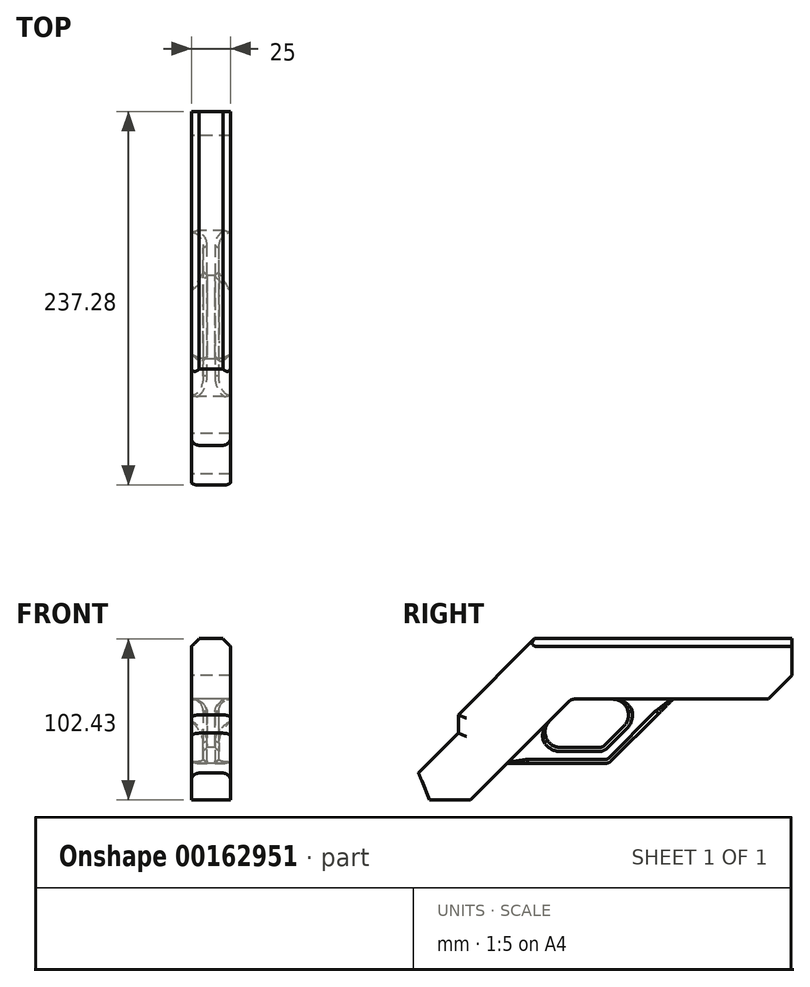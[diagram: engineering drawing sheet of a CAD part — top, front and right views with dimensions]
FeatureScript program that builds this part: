
annotation { "Feature Type Name" : "Feature", "Feature Type Description" : "" }
export const myFeature = defineFeature(function(context is Context, id is Id, definition is map)
    precondition{}
    {
        {
            var Q0;
            Q0=qCreatedBy(makeId("Right.planeOp"),FACE);
            var sketch = newSketch(context, id + "F0", { "sketchPlane" : qUnion([Q0])});
            skLineSegment(sketch, "E0", {"start": v(-96.29, 0) * mm, "end": v(-96.29, 15) * mm});
            skLineSegment(sketch, "E1", {"start": v(-96.29, 15) * mm, "end": v(75.64, 15) * mm});
            skLineSegment(sketch, "E2", {"start": v(75.64, 15) * mm, "end": v(75.64, 0) * mm});
            skLineSegment(sketch, "E3", {"start": v(75.64, 0) * mm, "end": v(60.55, -15) * mm});
            skLineSegment(sketch, "E4", {"start": v(60.55, -15) * mm, "end": v(0, -15) * mm});
            skLineSegment(sketch, "E5", {"start": v(0, -15) * mm, "end": v(-10, -25) * mm});
            skLineSegment(sketch, "E6", {"start": v(-10, -25) * mm, "end": v(-96.29, -25) * mm});
            skLineSegment(sketch, "E7", {"start": v(-96.29, -25) * mm, "end": v(-96.29, 0) * mm});
            skLineSegment(sketch, "E8", {"start": v(-96.29, 15) * mm, "end": v(-136.29, -25) * mm});
            skLineSegment(sketch, "E9", {"start": v(-136.29, -25) * mm, "end": v(-136.29, -36.6) * mm});
            skLineSegment(sketch, "E10", {"start": v(-136.29, -36.6) * mm, "end": v(-178.71, -79.02) * mm});
            skLineSegment(sketch, "E11", {"start": v(-178.71, -79.02) * mm, "end": v(-128.71, -79.02) * mm});
            skLineSegment(sketch, "E12", {"start": v(-128.71, -79.02) * mm, "end": v(-74.7, -25) * mm});
            skLineSegment(sketch, "E13", {"start": v(-10, -25) * mm, "end": v(-40.76, -55.76) * mm});
            skLineSegment(sketch, "E14", {"start": v(-40.76, -55.76) * mm, "end": v(-105.46, -55.76) * mm});
            skLineSegment(sketch, "E15", {"start": v(-24.14, -25) * mm, "end": v(-44.9, -45.76) * mm});
            skLineSegment(sketch, "E16", {"start": v(-44.9, -45.76) * mm, "end": v(-95.46, -45.76) * mm});
            skLineSegment(sketch, "E17", {"start": v(-96.29, 15) * mm, "end": v(-87.88, 23.41) * mm});
            skLineSegment(sketch, "E18", {"start": v(-87.88, 23.41) * mm, "end": v(75.64, 23.41) * mm});
            skLineSegment(sketch, "E19", {"start": v(75.64, 23.41) * mm, "end": v(75.64, 15) * mm});
            skLineSegment(sketch, "E20", {"start": v(-74.7, -25) * mm, "end": v(-64.7, -15) * mm});
            skLineSegment(sketch, "E21", {"start": v(-64.7, -15) * mm, "end": v(0, -15) * mm});
            skLineSegment(sketch, "E22", {"start": v(-24.14, -25) * mm, "end": v(-14.14, -15) * mm});
            skSolve(sketch);
        }
        {
            var Q0;
            Q0=makeQuery(id+"F0.imprint","IMPRINT",FACE,{"disambiguationData":[TD([[makeQuery(id+"F0.imprint","IMPRINT",EDGE,{"derivedFrom":sQuery(id+"F0.wireOp",EDGE,"E0")}),1.0]])]});
            var Q1;
            Q1=makeQuery(id+"F0.imprint","IMPRINT",FACE,{"disambiguationData":[TD([[makeQuery(id+"F0.imprint","IMPRINT",EDGE,{"derivedFrom":sQuery(id+"F0.wireOp",EDGE,"E0")}),-1.0]])]});
            var Q2;
            {var subQ1=sQuery(id+"F0.wireOp",EDGE,"E13");Q2=makeQuery(id+"F0.imprint","IMPRINT",FACE,{"disambiguationData":[TD([[makeQuery(id+"F0.imprint","IMPRINT",EDGE,{"derivedFrom":subQ1}),-1.0]])]});}
            var Q3;
            Q3=makeQuery(id+"F0.imprint","IMPRINT",FACE,{"disambiguationData":[TD([[makeQuery(id+"F0.imprint","IMPRINT",EDGE,{"derivedFrom":sQuery(id+"F0.wireOp",EDGE,"E1")}),1.0]])]});
            var Q4;
            {var subQ0=sQuery(id+"F0.wireOp",EDGE,"E5");Q4=makeQuery(id+"F0.imprint","IMPRINT",FACE,{"disambiguationData":[TD([[makeQuery(id+"F0.imprint","IMPRINT",EDGE,{"derivedFrom":subQ0}),-1.0]])]});}
            extrude(context, id + "F1", {"entities" : qUnion([Q0, Q1, Q2, Q3, Q4]), "depth" : 12.5 * mm});
        }
        {
            var Q0;
            Q0=makeQuery(id+"F1.opExtrude","CAP_EDGE",EDGE,{"disambiguationData":[OSD([sQuery(id+"F0.wireOp",EDGE,"E18")])],"isStart":false});
            chamfer(context, id + "F2", {"entities" : qUnion([Q0]), "width" : 5 * mm, "tangentPropagation" : true});
        }
        {
            var Q0;
            {var subQ0=makeQuery(id+"F1.opExtrude","SWEPT_EDGE",EDGE,{"disambiguationData":[OSD([sQuery(id+"F0.wireOp",EDGE,"E10"),sQuery(id+"F0.wireOp",EDGE,"E11")])]});Q0=makeQuery(id+"F9.boolean.opBoolean","MERGE",EDGE,{"derivedFrom":[subQ0,makeQuery(id+"F9.opPattern","COPY",EDGE,{"derivedFrom":subQ0,"instanceName":"1"})]});}
            chamfer(context, id + "F3", {"entities" : qUnion([Q0]), "width" : 10 * mm, "tangentPropagation" : true});
        }
        {
            var Q0;
            {var subQ0=makeQuery(id+"F1.opExtrude","SWEPT_EDGE",EDGE,{"disambiguationData":[OSD([sQuery(id+"F0.wireOp",EDGE,"E12"),sQuery(id+"F0.wireOp",EDGE,"E16")])]});Q0=makeQuery(id+"F9.boolean.opBoolean","MERGE",EDGE,{"derivedFrom":[subQ0,makeQuery(id+"F9.opPattern","COPY",EDGE,{"derivedFrom":subQ0,"instanceName":"1"})]});}
            var Q1;
            {var subQ0=makeQuery(id+"F1.opExtrude","SWEPT_EDGE",EDGE,{"disambiguationData":[OSD([sQuery(id+"F0.wireOp",EDGE,"E21"),sQuery(id+"F0.wireOp",EDGE,"E22")])]});Q1=makeQuery(id+"F9.boolean.opBoolean","MERGE",EDGE,{"derivedFrom":[subQ0,makeQuery(id+"F9.opPattern","COPY",EDGE,{"derivedFrom":subQ0,"instanceName":"1"})]});}
            fillet(context, id + "F4", {"entities" : qUnion([Q0, Q1]), "radius" : 10 * mm, "tangentPropagation" : true, "allowEdgeOverflow" : false});
        }
        {
            var Q0;
            Q0=makeQuery(id+"F1.opExtrude","CAP_FACE",FACE,{"disambiguationData":[OSD([sQuery(id+"F0.wireOp",EDGE,"E2"),sQuery(id+"F0.wireOp",EDGE,"E3"),sQuery(id+"F0.wireOp",EDGE,"E4"),sQuery(id+"F0.wireOp",EDGE,"E5"),sQuery(id+"F0.wireOp",EDGE,"E8"),sQuery(id+"F0.wireOp",EDGE,"E9"),sQuery(id+"F0.wireOp",EDGE,"E10"),sQuery(id+"F0.wireOp",EDGE,"E11"),sQuery(id+"F0.wireOp",EDGE,"E12"),sQuery(id+"F0.wireOp",EDGE,"E13"),sQuery(id+"F0.wireOp",EDGE,"E14"),sQuery(id+"F0.wireOp",EDGE,"E15"),sQuery(id+"F0.wireOp",EDGE,"E16"),sQuery(id+"F0.wireOp",EDGE,"E17"),sQuery(id+"F0.wireOp",EDGE,"E18"),sQuery(id+"F0.wireOp",EDGE,"E19"),sQuery(id+"F0.wireOp",EDGE,"E20"),sQuery(id+"F0.wireOp",EDGE,"E21"),sQuery(id+"F0.wireOp",EDGE,"E22")])],"isStart":false});
            var sketch = newSketch(context, id + "F5", { "sketchPlane" : qUnion([Q0])});
            skLineSegment(sketch, "E23.0", {"start": v(-128.71, -79.02) * mm, "end": v(-105.46, -55.76) * mm});
            skLineSegment(sketch, "E24.0", {"start": v(-40.76, -55.76) * mm, "end": v(-105.46, -55.76) * mm});
            skLineSegment(sketch, "E25.0", {"start": v(0, -15) * mm, "end": v(-40.76, -55.76) * mm});
            skLineSegment(sketch, "E26.0", {"start": v(-78.39, -28.7) * mm, "end": v(-64.7, -15) * mm});
            skLineSegment(sketch, "E27", {"start": v(-105.46, -55.76) * mm, "end": v(-78.39, -28.7) * mm});
            skLineSegment(sketch, "E28", {"start": v(-64.7, -15) * mm, "end": v(0, -15) * mm});
            skSolve(sketch);
        }
        {
            var Q0;
            Q0=makeQuery(id+"F5.imprint","IMPRINT",FACE,{"disambiguationData":[TD([[makeQuery(id+"F5.imprint","IMPRINT",EDGE,{"derivedFrom":sQuery(id+"F5.wireOp",EDGE,"E24.0")}),-1.0]])]});
            extrude(context, id + "F6", {"entities" : qUnion([Q0]), "operationType" : NewBodyOperationType.REMOVE, "oppositeDirection" : true, "depth" : 7.5 * mm});
        }
        {
            var Q0;
            {var subQ0=sQuery(id+"F0.wireOp",EDGE,"E12");Q0=makeQuery(id+"F6.boolean.opBoolean","MERGE",EDGE,{"derivedFrom":[makeQuery(id+"F1.opExtrude","CAP_EDGE",EDGE,{"disambiguationData":[OSD([subQ0])],"isStart":false}),makeQuery(id+"F1.opExtrude","CAP_EDGE",EDGE,{"disambiguationData":[OSD([subQ0,sQuery(id+"F0.wireOp",EDGE,"E20")])],"isStart":false}),makeQuery(id+"F6.opExtrude","CAP_EDGE",EDGE,{"disambiguationData":[OSD([sQuery(id+"F5.wireOp",EDGE,"E27")])],"isStart":true})]});}
            var Q1;
            Q1=makeQuery(id+"F1.opExtrude","CAP_EDGE",EDGE,{"disambiguationData":[OSD([sQuery(id+"F0.wireOp",EDGE,"E10")])],"isStart":false});
            var Q2;
            Q2=makeQuery(id+"F1.opExtrude","CAP_EDGE",EDGE,{"disambiguationData":[OSD([sQuery(id+"F0.wireOp",EDGE,"E9")])],"isStart":false});
            var Q3;
            Q3=makeQuery(id+"F1.opExtrude","CAP_EDGE",EDGE,{"disambiguationData":[OSD([sQuery(id+"F0.wireOp",EDGE,"E8"),sQuery(id+"F0.wireOp",EDGE,"E17")])],"isStart":false});
            fillet(context, id + "F7", {"entities" : qUnion([Q0, Q1, Q2, Q3]), "radius" : 5 * mm, "tangentPropagation" : true, "allowEdgeOverflow" : false});
        }
        {
            var Q0;
            Q0=makeQuery(id+"F1.opExtrude","SWEPT_EDGE",EDGE,{"disambiguationData":[OSD([sQuery(id+"F0.wireOp",EDGE,"E13"),sQuery(id+"F0.wireOp",EDGE,"E14")])]});
            var Q1;
            Q1=makeQuery(id+"F1.opExtrude","SWEPT_EDGE",EDGE,{"disambiguationData":[OSD([sQuery(id+"F0.wireOp",EDGE,"E15"),sQuery(id+"F0.wireOp",EDGE,"E16")])]});
            var Q2;
            Q2=makeQuery(id+"F1.opExtrude","SWEPT_EDGE",EDGE,{"disambiguationData":[OSD([sQuery(id+"F0.wireOp",EDGE,"E20"),sQuery(id+"F0.wireOp",EDGE,"E21")])]});
            fillet(context, id + "F8", {"entities" : qUnion([Q0, Q1, Q2]), "radius" : 5 * mm, "tangentPropagation" : true, "allowEdgeOverflow" : false});
        }
        {
            var Q0;
            Q0=makeQuery(id+"F1.opExtrude","SWEPT_BODY",BODY,{"disambiguationData":[OSD([sQuery(id+"F0.wireOp",EDGE,"E1"),sQuery(id+"F0.wireOp",EDGE,"E2"),sQuery(id+"F0.wireOp",EDGE,"E3"),sQuery(id+"F0.wireOp",EDGE,"E4"),sQuery(id+"F0.wireOp",EDGE,"E5"),sQuery(id+"F0.wireOp",EDGE,"E6"),sQuery(id+"F0.wireOp",EDGE,"E8"),sQuery(id+"F0.wireOp",EDGE,"E9"),sQuery(id+"F0.wireOp",EDGE,"E10"),sQuery(id+"F0.wireOp",EDGE,"E11"),sQuery(id+"F0.wireOp",EDGE,"E12"),sQuery(id+"F0.wireOp",EDGE,"E13"),sQuery(id+"F0.wireOp",EDGE,"E14"),sQuery(id+"F0.wireOp",EDGE,"E15"),sQuery(id+"F0.wireOp",EDGE,"E16")])]});
            var Q1;
            Q1=qCreatedBy(makeId("Right.planeOp"),FACE);
            mirror(context, id + "F9", {"operationType" : NewBodyOperationType.ADD, "entities" : qUnion([Q0]), "mirrorPlane" : qUnion([Q1])});
        }
        {
            var Q0;
            Q0=makeQuery(id+"F6.boolean.opBoolean","COPY",EDGE,{"derivedFrom":makeQuery(id+"F6.opExtrude","CAP_EDGE",EDGE,{"disambiguationData":[OSD([sQuery(id+"F5.wireOp",EDGE,"E27")])],"isStart":false})});
            var Q1;
            Q1=makeQuery(id+"F9.opPattern","COPY",EDGE,{"derivedFrom":makeQuery(id+"F6.boolean.opBoolean","COPY",EDGE,{"derivedFrom":makeQuery(id+"F6.opExtrude","CAP_EDGE",EDGE,{"disambiguationData":[OSD([sQuery(id+"F5.wireOp",EDGE,"E27")])],"isStart":false})}),"instanceName":"1"});
            var Q2;
            Q2=makeQuery(id+"F9.opPattern","COPY",EDGE,{"derivedFrom":makeQuery(id+"F6.boolean.opBoolean","COPY",EDGE,{"derivedFrom":makeQuery(id+"F6.opExtrude","CAP_EDGE",EDGE,{"disambiguationData":[OSD([sQuery(id+"F5.wireOp",EDGE,"E28")])],"isStart":false})}),"instanceName":"1"});
            var Q3;
            Q3=makeQuery(id+"F6.boolean.opBoolean","COPY",EDGE,{"derivedFrom":makeQuery(id+"F6.opExtrude","CAP_EDGE",EDGE,{"disambiguationData":[OSD([sQuery(id+"F5.wireOp",EDGE,"E28")])],"isStart":false})});
            fillet(context, id + "F10", {"entities" : qUnion([Q0, Q1, Q2, Q3]), "radius" : 7.5 * mm, "tangentPropagation" : true, "allowEdgeOverflow" : false});
        }
        {
            var Q0;
            Q0=makeQuery(id+"F6.boolean.opBoolean","COPY",FACE,{"derivedFrom":makeQuery(id+"F6.opExtrude","CAP_FACE",FACE,{"disambiguationData":[OSD([sQuery(id+"F0.wireOp",EDGE,"E2"),sQuery(id+"F0.wireOp",EDGE,"E3"),sQuery(id+"F0.wireOp",EDGE,"E4"),sQuery(id+"F0.wireOp",EDGE,"E5"),sQuery(id+"F0.wireOp",EDGE,"E8"),sQuery(id+"F0.wireOp",EDGE,"E9"),sQuery(id+"F0.wireOp",EDGE,"E10"),sQuery(id+"F0.wireOp",EDGE,"E11"),sQuery(id+"F0.wireOp",EDGE,"E12"),sQuery(id+"F0.wireOp",EDGE,"E13"),sQuery(id+"F0.wireOp",EDGE,"E14"),sQuery(id+"F0.wireOp",EDGE,"E15"),sQuery(id+"F0.wireOp",EDGE,"E16"),sQuery(id+"F0.wireOp",EDGE,"E17"),sQuery(id+"F0.wireOp",EDGE,"E18"),sQuery(id+"F0.wireOp",EDGE,"E19"),sQuery(id+"F0.wireOp",EDGE,"E20"),sQuery(id+"F0.wireOp",EDGE,"E21"),sQuery(id+"F0.wireOp",EDGE,"E22"),sQuery(id+"F5.wireOp",EDGE,"E24.0"),sQuery(id+"F5.wireOp",EDGE,"E25.0"),sQuery(id+"F5.wireOp",EDGE,"E27"),sQuery(id+"F5.wireOp",EDGE,"E28")])],"isStart":false})});
            var Q1;
            Q1=makeQuery(id+"F9.opPattern","COPY",FACE,{"derivedFrom":makeQuery(id+"F6.boolean.opBoolean","COPY",FACE,{"derivedFrom":makeQuery(id+"F6.opExtrude","CAP_FACE",FACE,{"disambiguationData":[OSD([sQuery(id+"F0.wireOp",EDGE,"E2"),sQuery(id+"F0.wireOp",EDGE,"E3"),sQuery(id+"F0.wireOp",EDGE,"E4"),sQuery(id+"F0.wireOp",EDGE,"E5"),sQuery(id+"F0.wireOp",EDGE,"E8"),sQuery(id+"F0.wireOp",EDGE,"E9"),sQuery(id+"F0.wireOp",EDGE,"E10"),sQuery(id+"F0.wireOp",EDGE,"E11"),sQuery(id+"F0.wireOp",EDGE,"E12"),sQuery(id+"F0.wireOp",EDGE,"E13"),sQuery(id+"F0.wireOp",EDGE,"E14"),sQuery(id+"F0.wireOp",EDGE,"E15"),sQuery(id+"F0.wireOp",EDGE,"E16"),sQuery(id+"F0.wireOp",EDGE,"E17"),sQuery(id+"F0.wireOp",EDGE,"E18"),sQuery(id+"F0.wireOp",EDGE,"E19"),sQuery(id+"F0.wireOp",EDGE,"E20"),sQuery(id+"F0.wireOp",EDGE,"E21"),sQuery(id+"F0.wireOp",EDGE,"E22"),sQuery(id+"F5.wireOp",EDGE,"E24.0"),sQuery(id+"F5.wireOp",EDGE,"E25.0"),sQuery(id+"F5.wireOp",EDGE,"E27"),sQuery(id+"F5.wireOp",EDGE,"E28")])],"isStart":false})}),"instanceName":"1"});
            chamfer(context, id + "F11", {"entities" : qUnion([Q0, Q1]), "width" : 2.5 * mm, "tangentPropagation" : true});
        }
    });
